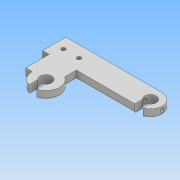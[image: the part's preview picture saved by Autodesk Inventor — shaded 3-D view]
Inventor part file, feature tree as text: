
AUTODESK INVENTOR PART (.ipt)
format: ipt  version: 2017 (Build 210142000, 142)  size: 182,272 bytes
history: native  units: mm
features: extrude x6, sketch x6, plane x1, fillet x1
ambient origin geometry x8: Origin, YZ Plane, XZ Plane, XY Plane, X Axis, Y Axis, Z Axis, Center Point
bodies: Solid1 (feature_tree)
feature tree (14):
  extrude  "Extrusion1"  Depth=18.0mm
  extrude  "Extrusion2"  Depth=18.0mm
  extrude  "Extrusion3"  Depth=18.0mm
  plane  "Work Plane1"
  extrude  "Extrusion4"  Depth=74.0mm
  fillet  "Fillet3"  Radius=21.0mm
  extrude  "Extrusion5"  Depth=6.0mm
  extrude  "Extrusion6"  Depth=6.0mm TaperAngle=0.0deg
  sketch  "Sketch1"  dims[d0=5.0mm d1=18.0mm]
  sketch  "Sketch2"  dims[d2=21.0mm d3=18.0mm]
  sketch  "Sketch3"  dims[d4=48.0mm d5=18.0mm]
  sketch  "Sketch4"  dims[d6=9.0mm d7=74.0mm d8=21.0mm]
  sketch  "Sketch5"  dims[d9=6.0mm d10=0.0mm d11=9.0mm]
  sketch  "Sketch6"  dims[d12=9.0mm d13=6.0mm d14=0.0mm d16=3.0mm d17=3.0mm d18=6.0mm d19=0.0mm d21=-83.0mm d22=3.0mm d23=18.0mm d24=0.0mm d25=1.0mm d26=3.0mm d27=3.0mm d28=5.0mm d29=0.0mm d30=6.0mm d31=6.0mm d32=6.0mm d33=11.0mm d34=10.0mm d35=0.0mm]
